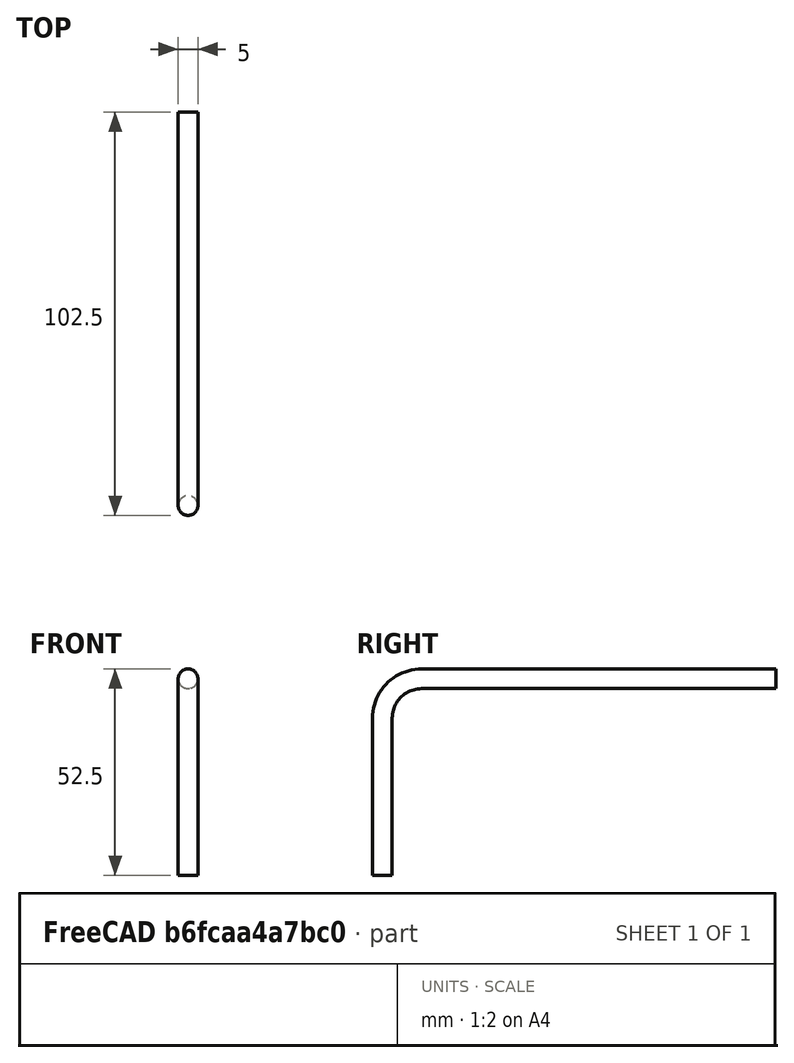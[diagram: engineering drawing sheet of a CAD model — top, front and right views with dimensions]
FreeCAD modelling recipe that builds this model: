
FCSTD DOCUMENT  (FreeCAD 0.19RUnknown)
Label: Probe
License: All rights reserved
LicenseURL: http://en.wikipedia.org/wiki/All_rights_reserved
objects: Sketcher::SketchObject×2, PartDesign::AdditivePipe×1, PartDesign::Body×1
note: 5 computed .brp shape members not serialized (recipe doc carries the construction recipe); baked Part::Feature solids carry a one-line shape summary decoded from their .brp

FEATURE [Sketcher::SketchObject] Sketch  label="ContactZoneSketch"
  FullyConstrained = true
  MapMode = 5
  Support = -> [XY_Plane]
  sketch-geometry (1):
    g0: Circle CenterX=0 CenterY=0 CenterZ=0 NormalX=0 NormalY=0 NormalZ=1 AngleXU=0 Radius=2.5
  constraints (2):
    c: Coincident(g-1,g0)
    c: Diameter(g0) = 5
FEATURE [Sketcher::SketchObject] Sketch001  label="ProbePath"
  FullyConstrained = true
  MapMode = 5
  Placement = pos=(0,0,0) rot=(0.57735,0.57735,0.57735;2.0944rad)
  Support = -> [YZ_Plane]
  sketch-geometry (3):
    g0: LineSegment StartX=0 StartY=0 StartZ=0 EndX=0 EndY=40 EndZ=0
    g1: ArcOfCircle CenterX=10 CenterY=40 CenterZ=0 NormalX=0 NormalY=0 NormalZ=1 AngleXU=0 Radius=10 StartAngle=1.5708 EndAngle=3.14159
    g2: LineSegment StartX=10 StartY=50 StartZ=0 EndX=100 EndY=50 EndZ=0
  constraints (8):
    c: Coincident(g0,g-1)
    c: Tangent(g0,g1) = 1.5708
    c: Tangent(g2,g1) = 1.5708
    c: DistanceY(g-1,g2) = 50
    c: DistanceX(g-1,g2) = 100
    c: Radius(g1) = 10
    c: Vertical(g0)
    c: Horizontal(g2)
FEATURE [PartDesign::AdditivePipe] AdditivePipe
  AuxilleryCurvelinear = true
  AuxillerySpineTangent = false
  Binormal = (0,0,0)
  Mode = 0
  Profile = -> Sketch
  Spine = -> Sketch001
  SpineTangent = false
  Transformation = 0
  Transition = 0
FEATURE [PartDesign::Body] Body
  Group = -> [Sketch,Sketch001,AdditivePipe]
  Origin = -> Origin
  Tip = -> AdditivePipe
